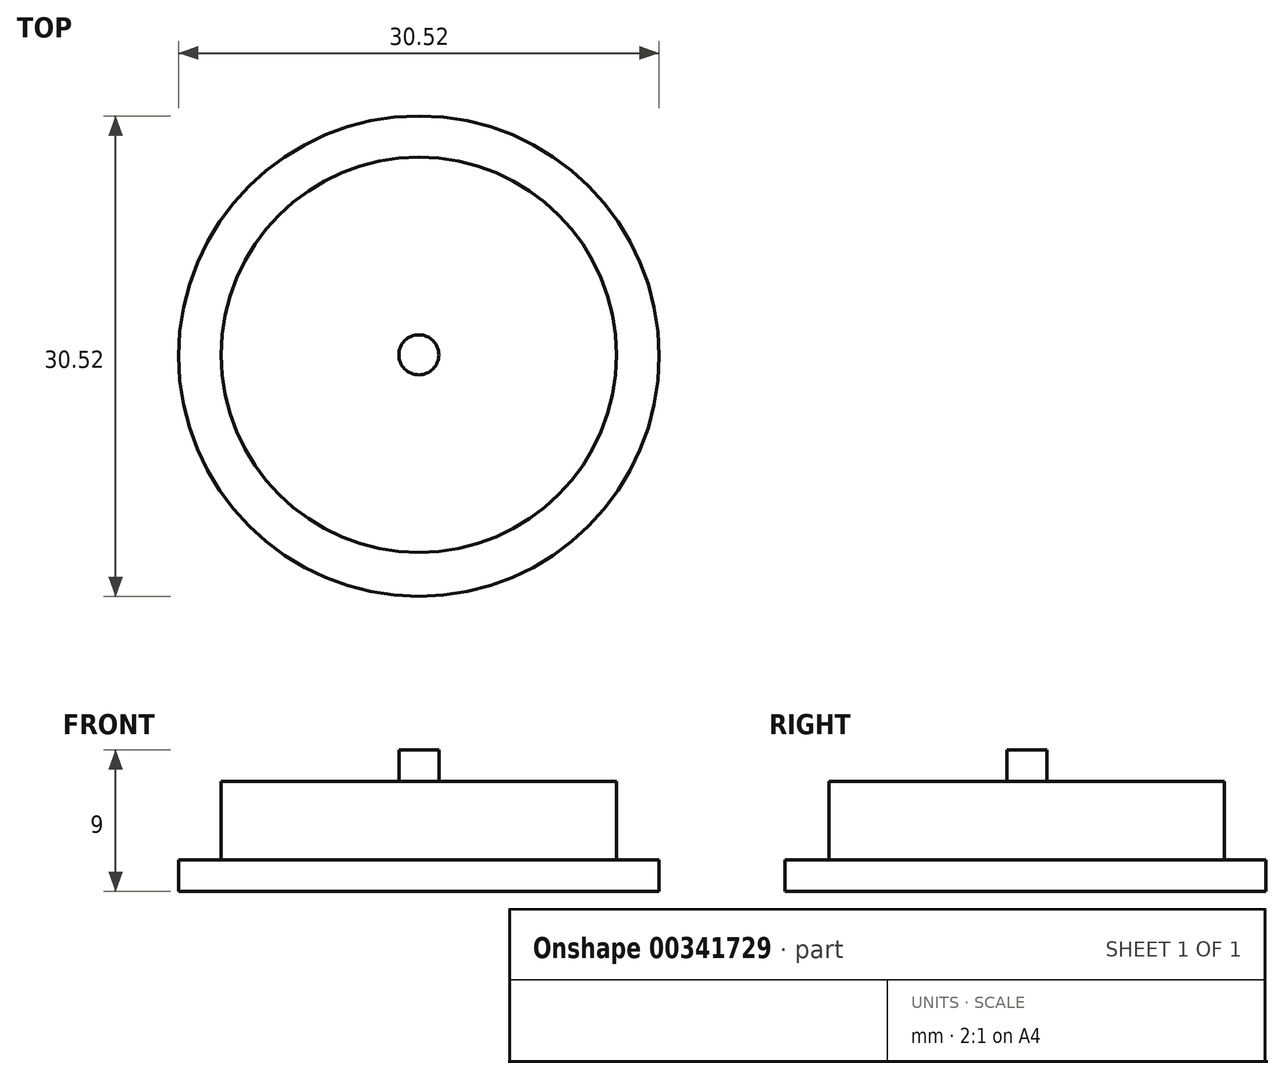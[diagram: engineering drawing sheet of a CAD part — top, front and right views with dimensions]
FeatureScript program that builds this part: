
annotation { "Feature Type Name" : "Feature", "Feature Type Description" : "" }
export const myFeature = defineFeature(function(context is Context, id is Id, definition is map)
    precondition{}
    {
        {
            var Q0;
            Q0=qCreatedBy(makeId("Top.planeOp"),FACE);
            var sketch = newSketch(context, id + "F0", { "sketchPlane" : qUnion([Q0])});
            skCircle(sketch, "E0", {"center": v(0, 6.5) * mm, "radius": 12.56 * mm});
            skSolve(sketch);
        }
        {
            var Q0;
            Q0=qCreatedBy(makeId("Top.planeOp"),FACE);
            var sketch = newSketch(context, id + "F1", { "sketchPlane" : qUnion([Q0])});
            skCircle(sketch, "E1", {"center": v(0, 6.41) * mm, "radius": 15.26 * mm});
            skSolve(sketch);
        }
        {
            var Q0;
            Q0=makeQuery(id+"F0.imprint","IMPRINT",FACE,{"disambiguationData":[TD([[makeQuery(id+"F0.imprint","IMPRINT",EDGE,{"derivedFrom":sQuery(id+"F0.wireOp",EDGE,"E0")}),1.0]])]});
            extrude(context, id + "F2", {"entities" : qUnion([Q0]), "depth" : 7 * mm});
        }
        {
            var Q0;
            Q0=makeQuery(id+"F1.imprint","IMPRINT",FACE,{"disambiguationData":[TD([[makeQuery(id+"F1.imprint","IMPRINT",EDGE,{"derivedFrom":sQuery(id+"F1.wireOp",EDGE,"E1")}),1.0]])]});
            extrude(context, id + "F3", {"entities" : qUnion([Q0]), "operationType" : NewBodyOperationType.ADD, "depth" : 2 * mm});
        }
        {
            var Q0;
            Q0=makeQuery(id+"F2.opExtrude","CAP_FACE",FACE,{"disambiguationData":[OSD([sQuery(id+"F0.wireOp",EDGE,"E0")])],"isStart":false});
            var sketch = newSketch(context, id + "F4", { "sketchPlane" : qUnion([Q0])});
            skCircle(sketch, "E2", {"center": v(0, 6.5) * mm, "radius": 1.27 * mm});
            skSolve(sketch);
        }
        {
            var Q0;
            Q0 = qSketchRegion(id + "F4", true);
            extrude(context, id + "F5", {"entities" : qUnion([Q0]), "operationType" : NewBodyOperationType.ADD, "depth" : 2 * mm});
        }
    });
